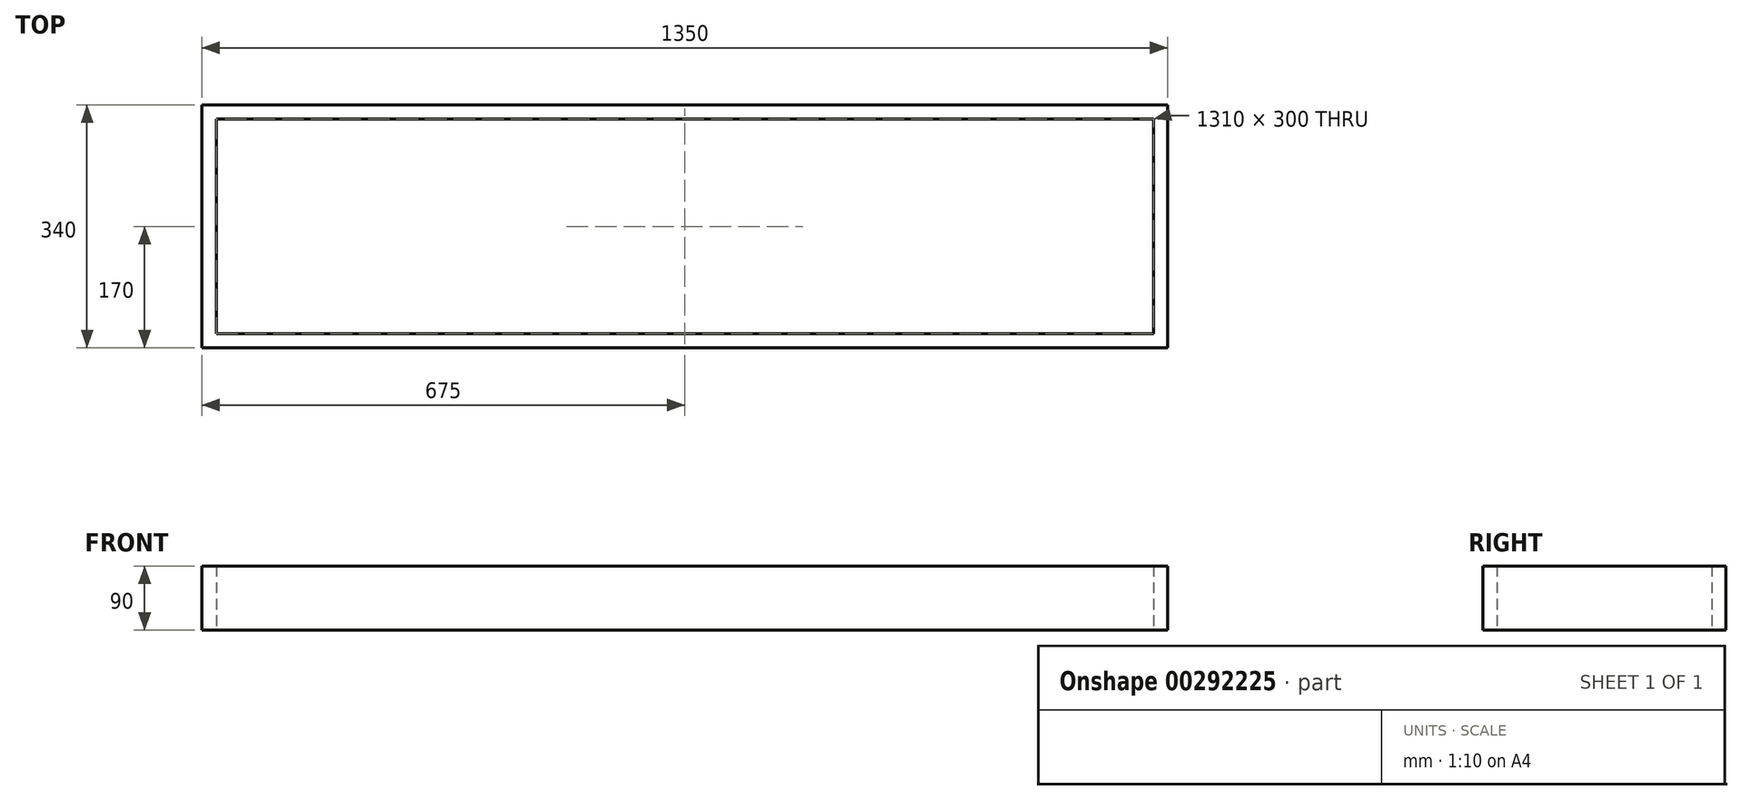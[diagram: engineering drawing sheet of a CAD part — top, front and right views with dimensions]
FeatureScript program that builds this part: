
annotation { "Feature Type Name" : "Feature", "Feature Type Description" : "" }
export const myFeature = defineFeature(function(context is Context, id is Id, definition is map)
    precondition{}
    {
        {
            var Q0;
            Q0=qCreatedBy(makeId("Top.planeOp"),FACE);
            var sketch = newSketch(context, id + "F0", { "sketchPlane" : qUnion([Q0])});
            skLineSegment(sketch, "E0.bottom", {"start": v(675, 170) * mm, "end": v(-675, 170) * mm});
            skLineSegment(sketch, "E0.top", {"start": v(675, -170) * mm, "end": v(-675, -170) * mm});
            skLineSegment(sketch, "E0.left", {"start": v(675, 170) * mm, "end": v(675, -170) * mm});
            skLineSegment(sketch, "E0.right", {"start": v(-675, 170) * mm, "end": v(-675, -170) * mm});
            skPoint(sketch, "E0.middle", {"position": v(0, 0) * mm});
            skLineSegment(sketch, "E1.0", {"start": v(655, 150) * mm, "end": v(-655, 150) * mm});
            skLineSegment(sketch, "E1.1", {"start": v(655, 150) * mm, "end": v(655, -150) * mm});
            skLineSegment(sketch, "E1.2", {"start": v(655, -150) * mm, "end": v(-655, -150) * mm});
            skLineSegment(sketch, "E1.3", {"start": v(-655, 150) * mm, "end": v(-655, -150) * mm});
            skSolve(sketch);
        }
        {
            var Q0;
            Q0 = qSketchRegion(id + "F0", true);
            extrude(context, id + "F1", {"entities" : qUnion([Q0]), "depth" : 90 * mm});
        }
    });
